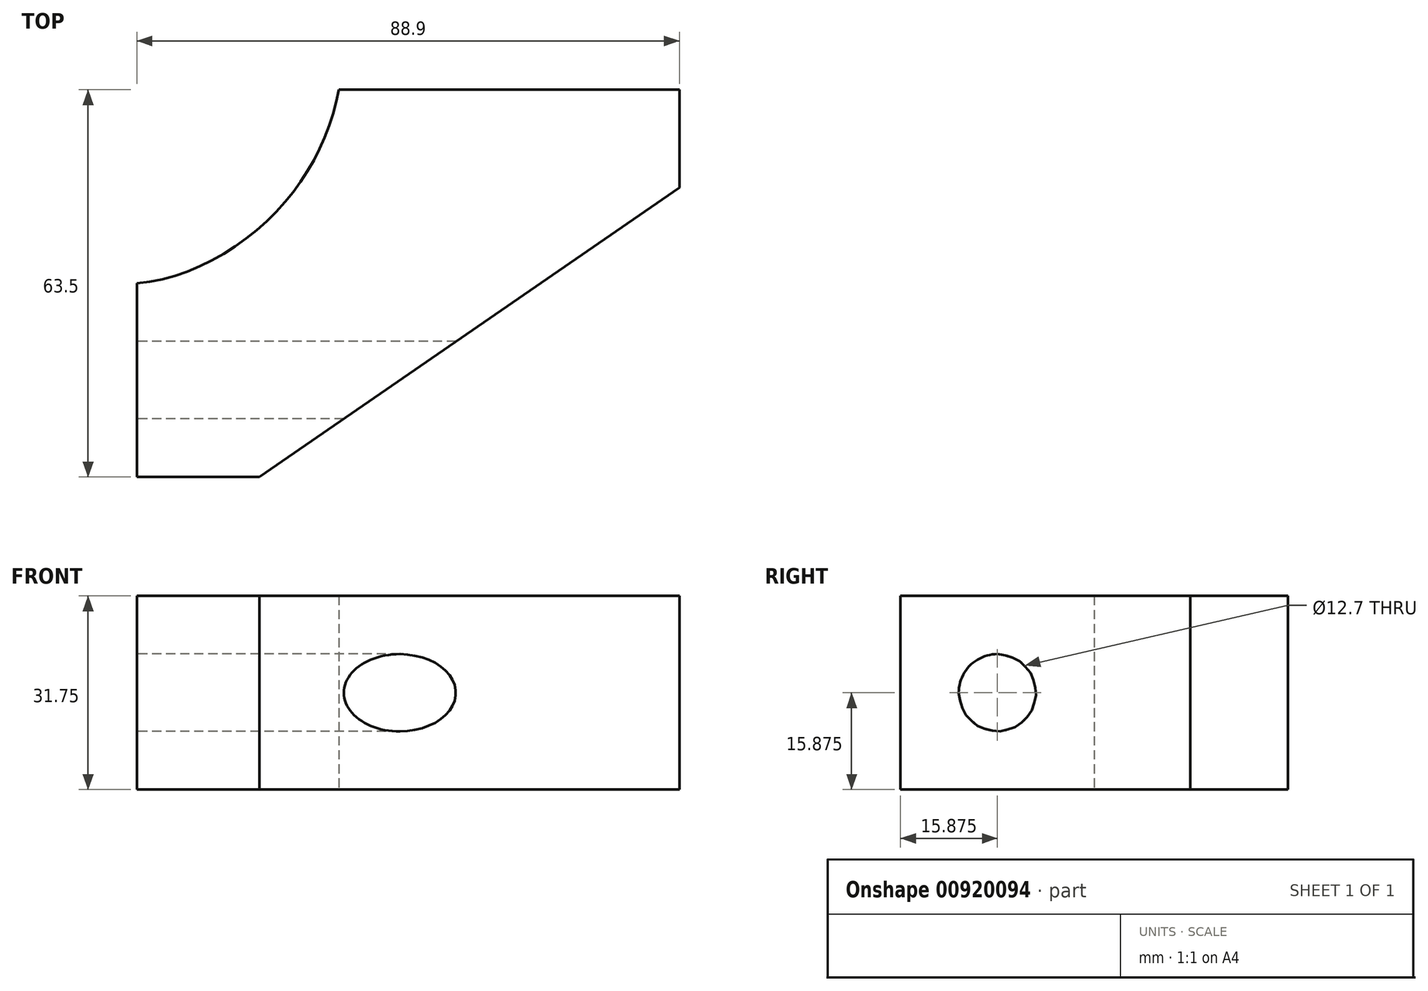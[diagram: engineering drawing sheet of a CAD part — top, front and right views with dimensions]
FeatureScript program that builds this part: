
annotation { "Feature Type Name" : "Feature", "Feature Type Description" : "" }
export const myFeature = defineFeature(function(context is Context, id is Id, definition is map)
    precondition{}
    {
        {
            var Q0;
            Q0=qCreatedBy(makeId("Top.planeOp"),FACE);
            var sketch = newSketch(context, id + "F0", { "sketchPlane" : qUnion([Q0])});
            skLineSegment(sketch, "E0.bottom", {"start": v(-42.9, 36.05) * mm, "end": v(46, 36.05) * mm});
            skLineSegment(sketch, "E0.top", {"start": v(-42.9, -27.45) * mm, "end": v(46, -27.45) * mm});
            skLineSegment(sketch, "E0.left", {"start": v(-42.9, 36.05) * mm, "end": v(-42.9, -27.45) * mm});
            skLineSegment(sketch, "E0.right", {"start": v(46, 36.05) * mm, "end": v(46, -27.45) * mm});
            skLineSegment(sketch, "E1", {"start": v(-42.9, 36.05) * mm, "end": v(-42.9, 4.3) * mm});
            skFitSpline(sketch, "E2", {"points": [v(-42.9, 4.3) * mm, v(-20.46, 15.66) * mm, v(-9.83, 36.05) * mm], "startDerivative": vector(48, 3.6) * mm, "endDerivative": vector(8.57, 46.24) * mm});
            skLineSegment(sketch, "E3", {"start": v(46, 20.03) * mm, "end": v(-22.8, -27.45) * mm});
            skSolve(sketch);
        }
        {
            var Q0;
            {var subQ4=sQuery(id+"F0.wireOp",EDGE,"E2");Q0=makeQuery(id+"F0.imprint","IMPRINT",FACE,{"disambiguationData":[TD([[makeQuery(id+"F0.imprint","IMPRINT",EDGE,{"derivedFrom":subQ4}),-1.0]])]});}
            extrude(context, id + "F1", {"entities" : qUnion([Q0]), "depth" : 31.75 * mm, "offsetDistance" : 25.4 * mm});
        }
        {
            var Q0;
            Q0=makeQuery(id+"F1.opExtrude","SWEPT_FACE",FACE,{"disambiguationData":[OSD([sQuery(id+"F0.wireOp",EDGE,"E0.left")])]});
            var sketch = newSketch(context, id + "F2", { "sketchPlane" : qUnion([Q0])});
            skLineSegment(sketch, "E4", {"start": v(11.57, 31.75) * mm, "end": v(11.57, 0) * mm});
            skCircle(sketch, "E5", {"center": v(11.57, 15.88) * mm, "radius": 6.35 * mm});
            skSolve(sketch);
        }
        {
            var Q0;
            Q0=sQuery(id+"F2.wireOp",VERTEX,"E5.center");
            var Q1;
            Q1=makeQuery(id+"F1.opExtrude","SWEPT_BODY",BODY,{"disambiguationData":[OSD([sQuery(id+"F0.wireOp",EDGE,"E0.bottom"),sQuery(id+"F0.wireOp",EDGE,"E0.top"),sQuery(id+"F0.wireOp",EDGE,"E0.left"),sQuery(id+"F0.wireOp",EDGE,"E0.right"),sQuery(id+"F0.wireOp",EDGE,"E2"),sQuery(id+"F0.wireOp",EDGE,"E3")])]});
            hole(context, id + "F3", {"style" : HoleStyle.SIMPLE, "endStyle" : HoleEndStyle.THROUGH, "holeDiameter" : 12.7 * mm, "majorDiameter" : 6.35 * mm, "isTappedThrough" : true, "tappedDepth" : 12.7 * mm, "tapClearance" : 3, "locations" : qUnion([Q0]), "scope" : qUnion([Q1])});
        }
    });
